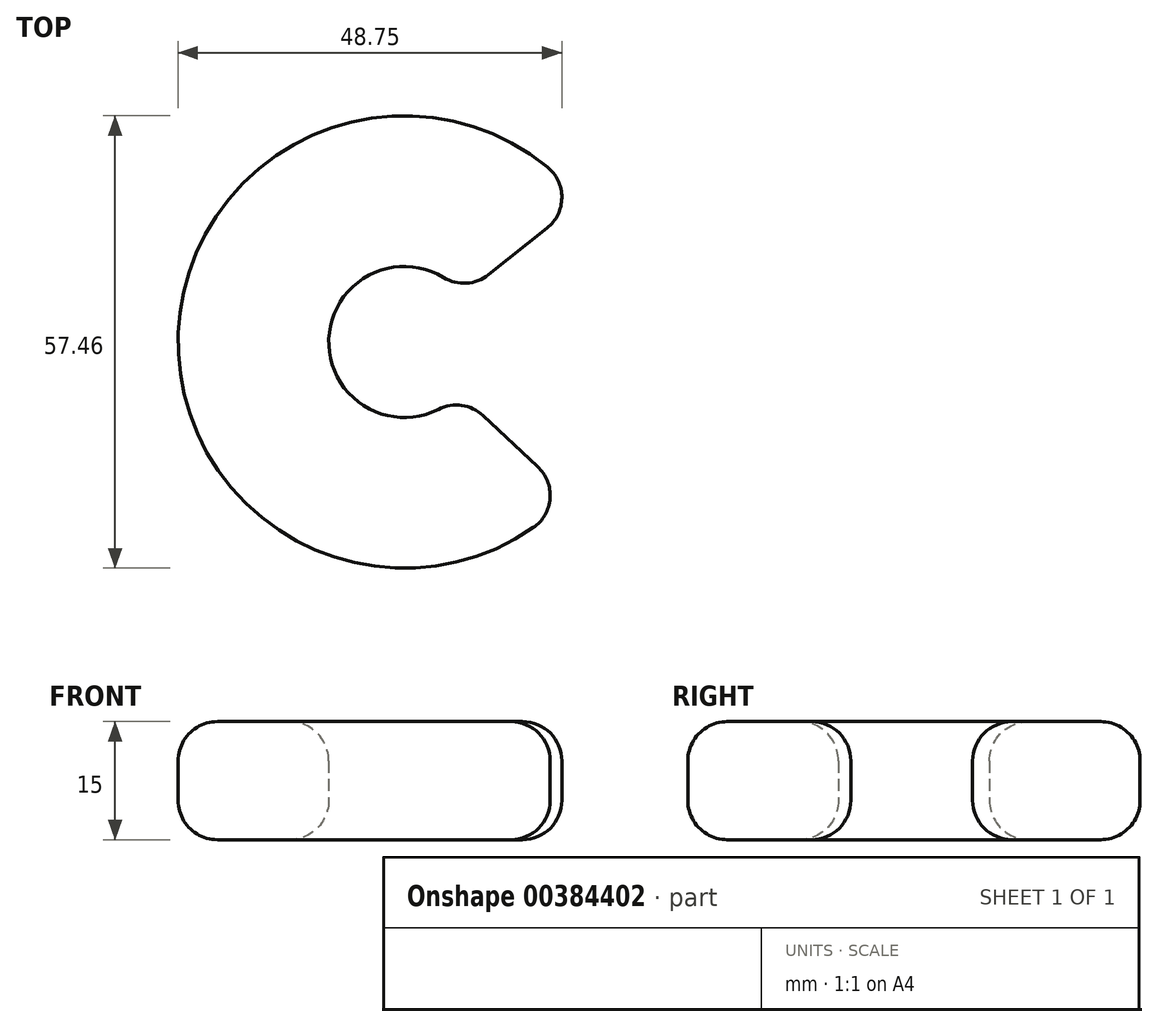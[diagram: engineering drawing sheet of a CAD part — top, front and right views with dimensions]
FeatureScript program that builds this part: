
annotation { "Feature Type Name" : "Feature", "Feature Type Description" : "" }
export const myFeature = defineFeature(function(context is Context, id is Id, definition is map)
    precondition{}
    {
        {
            var Q0;
            Q0=qCreatedBy(makeId("Top.planeOp"),FACE);
            var sketch = newSketch(context, id + "F0", { "sketchPlane" : qUnion([Q0])});
            skCircle(sketch, "E0", {"center": v(0, 0) * mm, "radius": 28.73 * mm});
            skCircle(sketch, "E1", {"center": v(0, 0) * mm, "radius": 9.6 * mm});
            skLineSegment(sketch, "E2", {"start": v(0, 0) * mm, "end": v(22.46, 17.9) * mm});
            skLineSegment(sketch, "E3", {"start": v(0, 0) * mm, "end": v(20.99, -19.61) * mm});
            skSolve(sketch);
        }
        {
            var Q0;
            {var subQ0=sQuery(id+"F0.wireOp",EDGE,"E2");var subQ1=sQuery(id+"F0.wireOp",EDGE,"E0");var subQ2=makeQuery(id+"F0.imprint","INTERSECT",VERTEX,{"derivedFrom":[subQ1,subQ0]});Q0=makeQuery(id+"F0.imprint","IMPRINT",FACE,{"disambiguationData":[TD([[makeQuery(id+"F0.imprint","IMPRINT",EDGE,{"disambiguationData":[TD([[subQ2,-1.0]])],"derivedFrom":subQ1}),1.0]])]});}
            extrude(context, id + "F1", {"entities" : qUnion([Q0]), "depth" : 15 * mm, "offsetDistance" : 25 * mm});
        }
        {
            var Q0;
            Q0=makeQuery(id+"F1.opExtrude","CAP_FACE",FACE,{"disambiguationData":[OSD([sQuery(id+"F0.wireOp",EDGE,"E0"),sQuery(id+"F0.wireOp",EDGE,"E1"),sQuery(id+"F0.wireOp",EDGE,"E2"),sQuery(id+"F0.wireOp",EDGE,"E3")])],"isStart":false});
            var Q1;
            Q1=makeQuery(id+"F1.opExtrude","CAP_FACE",FACE,{"disambiguationData":[OSD([sQuery(id+"F0.wireOp",EDGE,"E0"),sQuery(id+"F0.wireOp",EDGE,"E1"),sQuery(id+"F0.wireOp",EDGE,"E2"),sQuery(id+"F0.wireOp",EDGE,"E3")])],"isStart":true});
            var Q2;
            Q2=makeQuery(id+"F1.opExtrude","SWEPT_FACE",FACE,{"disambiguationData":[OSD([sQuery(id+"F0.wireOp",EDGE,"E3")])]});
            var Q3;
            Q3=makeQuery(id+"F1.opExtrude","SWEPT_FACE",FACE,{"disambiguationData":[OSD([sQuery(id+"F0.wireOp",EDGE,"E2")])]});
            fillet(context, id + "F2", {"entities" : qUnion([Q0, Q1, Q2, Q3]), "radius" : 5 * mm, "tangentPropagation" : true, "allowEdgeOverflow" : false});
        }
    });
